# Revit family: 028.HW-25NW-20-30 Slim 150 (KP) (W)
name_source: partatom
category: Osprzęt hydrauliczny
revit_build: Autodesk Revit 2018 (Build: 20190510_1515(x64)
units: mm (PartAtom-declared; Revit-internal decimal feet)

## family parameters
Obiekt nadrzędny = Powierzchnia
Punkt obliczania pomieszczeń = Nie
Tnij formami wycięć po wczytaniu = Nie
Typ części = Normalny
Współdzielony = Nie
Wymiar okrągłego złącza = Użyj średnicy

## types (2) — shared parameters
Cabinet_Depth = 150 mm  [stored 0.492126 ft]
Cabinet_G_Depth = 150 mm  [stored 0.492126 ft]
Cabinet_G_Height = 795 mm  [stored 2.60827 ft]
Cabinet_G_Width = 230 mm  [stored 0.754593 ft]
Cabinet_Height = 795 mm  [stored 2.60827 ft]
Cabinet_Width = 795 mm  [stored 2.60827 ft]
D1 = 75 mm  [stored 0.246063 ft]
DN = 25 mm  [stored 0.082021 ft]
Flow = 60.0 L/s
H1 = 70 mm  [stored 0.229659 ft]
Hole_Depth = 160 mm  [stored 0.524934 ft]
Hole_Height = 1045 mm  [stored 3.42848 ft]
Hole_Width = 815 mm  [stored 2.67388 ft]
K_factor = 42
Model = HW-25NW-KP-20/30 SLIM150 W, RAL3000
Opis = http://gras.pl
Producent = GRAS PPPH
URL = http://www.gras.pl
W1 = 70 mm  [stored 0.229659 ft]
W2 = 40 mm  [stored 0.131234 ft]
cabinet_H/2+10 = 408 mm
picH = 60 mm  [stored 0.19685 ft]
zero-valued in all types: 0, Domyślna rzędna, Mounting_point, mounting_plane, zer0

## per-type parameters (varying)
| type | Cabinet_Material |
| HW-25NW-KP-20/30 SLIM150 W, RAL9010 | DC01, RAL9010 |
| HW-25NW-KP-20/30 SLIM150 W, RAL3000 | DC01, RAL3000 |

note: [stored X ft] marks values corroborated as IEEE doubles in the binary element streams (Revit-internal decimal feet)

## geometry (parser evidence)
native form markers: Blend x4
no freeform markers — native parametric forms only
